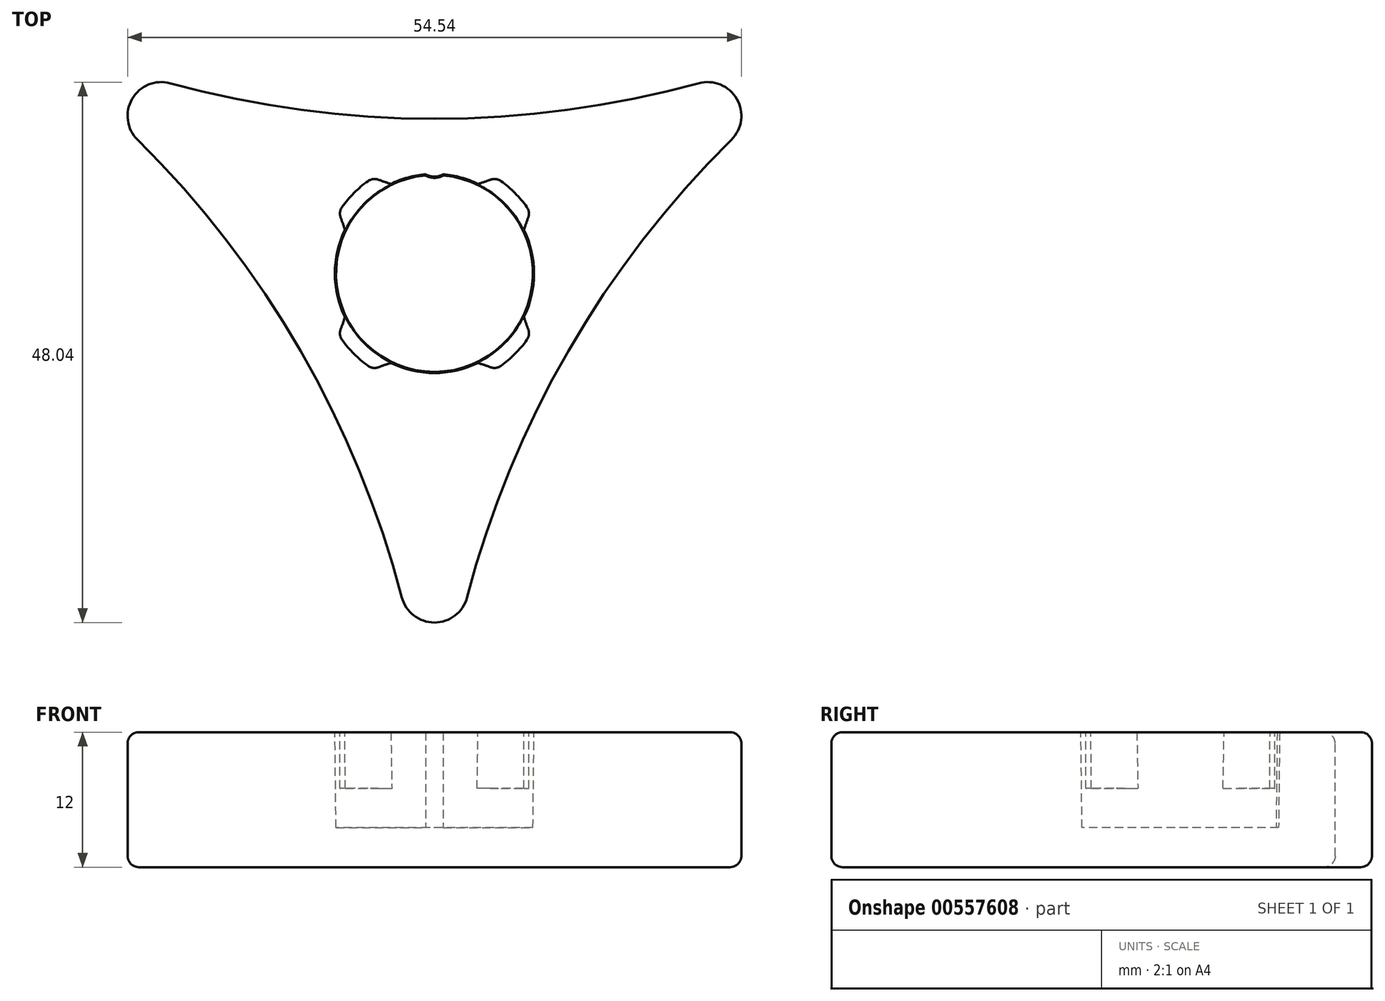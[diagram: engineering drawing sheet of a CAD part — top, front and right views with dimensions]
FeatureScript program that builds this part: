
annotation { "Feature Type Name" : "Feature", "Feature Type Description" : "" }
export const myFeature = defineFeature(function(context is Context, id is Id, definition is map)
    precondition{}
    {
        {
            assignVariable(context, id + "F0", {"name" : "height", "anyValue" : 8.5});
        }
        {
            assignVariable(context, id + "F1", {"name" : "middleThickness", "anyValue" : 3.5});
        }
        {
            var Q0;
            Q0=qCreatedBy(makeId("Top.planeOp"),FACE);
            var sketch = newSketch(context, id + "F2", { "sketchPlane" : qUnion([Q0])});
            skCircle(sketch, "E0", {"center": v(0, 0) * mm, "radius": 8.85 * mm});
            skSolve(sketch);
        }
        {
            var Q0;
            Q0=makeQuery(id+"F2.imprint","IMPRINT",FACE,{"disambiguationData":[TD([[makeQuery(id+"F2.imprint","IMPRINT",EDGE,{"derivedFrom":sQuery(id+"F2.wireOp",EDGE,"E0")}),1.0]])]});
            cPlane(context, id + "F3", {"entities" : qUnion([Q0]), "cplaneType" : CPlaneType.OFFSET, "offset" : (getVariable(context, 'height')) * mm, "width" : 150 * mm, "height" : 150 * mm});
        }
        {
            var Q0;
            Q0=makeQuery(id+"F2.imprint","IMPRINT",FACE,{"disambiguationData":[TD([[makeQuery(id+"F2.imprint","IMPRINT",EDGE,{"derivedFrom":sQuery(id+"F2.wireOp",EDGE,"E0")}),1.0]])]});
            var sketch = newSketch(context, id + "F4", { "sketchPlane" : qUnion([Q0])});
            skCircle(sketch, "E1", {"center": v(0, 0) * mm, "radius": 8.6 * mm, "construction": true});
            skArc(sketch, "E2", {"start": v(-0.78, 8.82) * mm, "mid": v(0, 8.6) * mm, "end": v(0.78, 8.82) * mm});
            skArc(sketch, "E3", {"start": v(0.78, 8.82) * mm, "mid": v(0, 8.85) * mm, "end": v(-0.78, 8.82) * mm});
            skSolve(sketch);
        }
        {
            var Q0;
            Q0=qCreatedBy(id+"F3.planeOp",FACE);
            var sketch = newSketch(context, id + "F5", { "sketchPlane" : qUnion([Q0])});
            skCircle(sketch, "E4", {"center": v(0, 0) * mm, "radius": 8.75 * mm});
            skSolve(sketch);
        }
        {
            var Q0;
            Q0=qCreatedBy(id+"F3.planeOp",FACE);
            var sketch = newSketch(context, id + "F6", { "sketchPlane" : qUnion([Q0])});
            skCircle(sketch, "E5", {"center": v(0, 0) * mm, "radius": 8.5 * mm, "construction": true});
            skArc(sketch, "E6", {"start": v(-0.77, 8.72) * mm, "mid": v(0, 8.5) * mm, "end": v(0.77, 8.72) * mm});
            skArc(sketch, "E7", {"start": v(0.77, 8.72) * mm, "mid": v(0, 8.75) * mm, "end": v(-0.77, 8.72) * mm});
            skSolve(sketch);
        }
        {
            var Q0;
            Q0 = qSketchRegion(id + "F2", true);
            var Q1;
            Q1 = qSketchRegion(id + "F5", true);
            loft(context, id + "F7", {"sheetProfilesArray" : [{ "sheetProfileEntities" : qUnion([Q0]) }, { "sheetProfileEntities" : qUnion([Q1]) }]});
        }
        {
            var Q1;
            Q1 = qSketchRegion(id + "F4", true);
            var Q2;
            Q2 = qSketchRegion(id + "F6", true);
            loft(context, id + "F8", {"operationType" : NewBodyOperationType.REMOVE, "sheetProfilesArray" : [{ "sheetProfileEntities" : qUnion([Q1]) }, { "sheetProfileEntities" : qUnion([Q2]) }]});
        }
        {
            var Q0;
            Q0=qCreatedBy(makeId("Front.planeOp"),FACE);
            var sketch = newSketch(context, id + "F9", { "sketchPlane" : qUnion([Q0])});
            skLineSegment(sketch, "E8", {"start": v(0, 0) * mm, "end": v(0, 8.15) * mm});
            skSolve(sketch);
        }
        {
            var Q0;
            Q0=qCreatedBy(makeId("Top.planeOp"),FACE);
            var sketch = newSketch(context, id + "F10", { "sketchPlane" : qUnion([Q0])});
            skCircle(sketch, "E9", {"center": v(0, 0) * mm, "radius": 13.75 * mm, "construction": true});
            skArc(sketch, "E10", {"start": v(-44.44, 25.66) * mm, "mid": v(0, 13.75) * mm, "end": v(44.44, 25.66) * mm});
            skArc(sketch, "E11.1.0", {"start": v(0, -51.32) * mm, "mid": v(-11.9, -6.88) * mm, "end": v(-44.44, 25.66) * mm});
            skArc(sketch, "E11.2.0", {"start": v(44.44, 25.66) * mm, "mid": v(11.9, -6.88) * mm, "end": v(0, -51.32) * mm});
            skSolve(sketch);
        }
        {
            var Q0;
            Q0 = qSketchRegion(id + "F10", true);
            extrude(context, id + "F11", {"entities" : qUnion([Q0]), "depth" : (getVariable(context, 'height') + getVariable(context, 'middleThickness')) * mm, "offsetDistance" : 25 * mm});
        }
        {
            var Q0;
            Q0=makeQuery(id+"F11.opExtrude","SWEPT_EDGE",EDGE,{"disambiguationData":[OSD([sQuery(id+"F10.wireOp",EDGE,"E10"),sQuery(id+"F10.wireOp",EDGE,"E11.2.0")])]});
            var Q1;
            Q1=makeQuery(id+"F11.opExtrude","SWEPT_EDGE",EDGE,{"disambiguationData":[OSD([sQuery(id+"F10.wireOp",EDGE,"E10"),sQuery(id+"F10.wireOp",EDGE,"E11.1.0")])]});
            var Q2;
            Q2=makeQuery(id+"F11.opExtrude","SWEPT_EDGE",EDGE,{"disambiguationData":[OSD([sQuery(id+"F10.wireOp",EDGE,"E11.1.0"),sQuery(id+"F10.wireOp",EDGE,"E11.2.0")])]});
            fillet(context, id + "F12", {"entities" : qUnion([Q0, Q1, Q2]), "radius" : 3 * mm, "tangentPropagation" : true, "allowEdgeOverflow" : false});
        }
        {
            var Q0;
            Q0=makeQuery(id+"F7.opLoft","SWEPT_BODY",BODY,{"disambiguationData":[OSD([makeQuery(id+"F2.imprint","IMPRINT",FACE,{"disambiguationData":[TD([[makeQuery(id+"F2.imprint","IMPRINT",EDGE,{"derivedFrom":sQuery(id+"F2.wireOp",EDGE,"E0")}),1.0]])]}),makeQuery(id+"F5.imprint","IMPRINT",FACE,{"disambiguationData":[TD([[makeQuery(id+"F5.imprint","IMPRINT",EDGE,{"derivedFrom":sQuery(id+"F5.wireOp",EDGE,"E4")}),1.0]])]})])]});
            var Q1;
            Q1=makeQuery(id+"F11.opExtrude","SWEPT_BODY",BODY,{"disambiguationData":[OSD([sQuery(id+"F10.wireOp",EDGE,"E10"),sQuery(id+"F10.wireOp",EDGE,"E11.1.0"),sQuery(id+"F10.wireOp",EDGE,"E11.2.0")])]});
            booleanBodies(context, id + "F13", {"operationType" : BooleanOperationType.SUBTRACTION, "tools" : qUnion([Q0]), "targets" : qUnion([Q1])});
        }
        {
            assignVariable(context, id + "F14", {"name" : "GoProKnobHeight", "anyValue" : 5});
        }
        {
            var Q0;
            Q0=makeQuery(id+"F11.opExtrude","CAP_FACE",FACE,{"disambiguationData":[OSD([sQuery(id+"F10.wireOp",EDGE,"E10"),sQuery(id+"F10.wireOp",EDGE,"E11.1.0"),sQuery(id+"F10.wireOp",EDGE,"E11.2.0")])],"isStart":true});
            var sketch = newSketch(context, id + "F15", { "sketchPlane" : qUnion([Q0])});
            skArc(sketch, "E12", {"start": v(5.9, -8.21) * mm, "mid": v(7.15, -7.15) * mm, "end": v(8.21, -5.9) * mm});
            skArc(sketch, "E13", {"start": v(-4.96, 8.33) * mm, "mid": v(0, 7.4) * mm, "end": v(4.96, 8.33) * mm});
            skArc(sketch, "E14.1.0", {"start": v(-8.33, -4.96) * mm, "mid": v(-7.4, 0) * mm, "end": v(-8.33, 4.96) * mm});
            skArc(sketch, "E14.2.0", {"start": v(4.96, -8.33) * mm, "mid": v(0, -7.4) * mm, "end": v(-4.96, -8.33) * mm});
            skArc(sketch, "E14.3.0", {"start": v(8.33, 4.96) * mm, "mid": v(7.4, 0) * mm, "end": v(8.33, -4.96) * mm});
            skPoint(sketch, "E15", {"position": v(5.44, 8.53) * mm});
            skPoint(sketch, "E16", {"position": v(5.44, -8.53) * mm});
            skArc(sketch, "E17.trimOffspring", {"start": v(-8.21, -5.9) * mm, "mid": v(-7.15, -7.15) * mm, "end": v(-5.9, -8.21) * mm});
            skArc(sketch, "E18.trimOffspring", {"start": v(-5.9, 8.21) * mm, "mid": v(-7.15, 7.15) * mm, "end": v(-8.21, 5.9) * mm});
            skArc(sketch, "E19.trimOffspring", {"start": v(8.21, 5.9) * mm, "mid": v(7.15, 7.15) * mm, "end": v(5.9, 8.21) * mm});
            skArc(sketch, "E20.filletArc", {"start": v(4.96, -8.33) * mm, "mid": v(5.45, -8.4) * mm, "end": v(5.9, -8.21) * mm});
            skPoint(sketch, "E21.visualSharp", {"position": v(8.53, -5.44) * mm});
            skArc(sketch, "E21.filletArc", {"start": v(8.21, -5.9) * mm, "mid": v(8.4, -5.45) * mm, "end": v(8.33, -4.96) * mm});
            skPoint(sketch, "E22.visualSharp", {"position": v(8.53, 5.44) * mm});
            skArc(sketch, "E22.filletArc", {"start": v(8.33, 4.96) * mm, "mid": v(8.4, 5.45) * mm, "end": v(8.21, 5.9) * mm});
            skArc(sketch, "E23.filletArc", {"start": v(5.9, 8.21) * mm, "mid": v(5.45, 8.4) * mm, "end": v(4.96, 8.33) * mm});
            skPoint(sketch, "E24.visualSharp", {"position": v(-5.44, 8.53) * mm});
            skArc(sketch, "E24.filletArc", {"start": v(-4.96, 8.33) * mm, "mid": v(-5.45, 8.4) * mm, "end": v(-5.9, 8.21) * mm});
            skPoint(sketch, "E25.visualSharp", {"position": v(-8.53, 5.44) * mm});
            skArc(sketch, "E25.filletArc", {"start": v(-8.21, 5.9) * mm, "mid": v(-8.4, 5.45) * mm, "end": v(-8.33, 4.96) * mm});
            skPoint(sketch, "E26.visualSharp", {"position": v(-8.53, -5.44) * mm});
            skArc(sketch, "E26.filletArc", {"start": v(-8.33, -4.96) * mm, "mid": v(-8.4, -5.45) * mm, "end": v(-8.21, -5.9) * mm});
            skPoint(sketch, "E27.visualSharp", {"position": v(-5.44, -8.53) * mm});
            skArc(sketch, "E27.filletArc", {"start": v(-5.9, -8.21) * mm, "mid": v(-5.45, -8.4) * mm, "end": v(-4.96, -8.33) * mm});
            skSolve(sketch);
        }
        {
            var Q0;
            Q0 = qSketchRegion(id + "F15", true);
            extrude(context, id + "F16", {"entities" : qUnion([Q0]), "operationType" : NewBodyOperationType.REMOVE, "oppositeDirection" : true, "depth" : (getVariable(context, 'GoProKnobHeight')) * mm, "offsetDistance" : 25 * mm});
        }
        {
            var Q0;
            Q0=makeQuery(id+"F11.opExtrude","CAP_FACE",FACE,{"disambiguationData":[OSD([sQuery(id+"F10.wireOp",EDGE,"E10"),sQuery(id+"F10.wireOp",EDGE,"E11.1.0"),sQuery(id+"F10.wireOp",EDGE,"E11.2.0")])],"isStart":true});
            cPlane(context, id + "F17", {"entities" : qUnion([Q0]), "cplaneType" : CPlaneType.OFFSET, "offset" : ((getVariable(context, 'height') + getVariable(context, 'middleThickness')) / 2) * mm, "oppositeDirection" : true, "width" : 150 * mm, "height" : 150 * mm});
        }
        {
            var Q0;
            Q0=qCreatedBy(id+"F17.planeOp",FACE);
            var sketch = newSketch(context, id + "F18", { "sketchPlane" : qUnion([Q0])});
            skLineSegment(sketch, "E28", {"start": v(0, 45.44) * mm, "end": v(0, -39.08) * mm, "construction": true});
            skSolve(sketch);
        }
        {
            var Q0;
            Q0=makeQuery(id+"F11.opExtrude","SWEPT_BODY",BODY,{"disambiguationData":[OSD([sQuery(id+"F10.wireOp",EDGE,"E10"),sQuery(id+"F10.wireOp",EDGE,"E11.1.0"),sQuery(id+"F10.wireOp",EDGE,"E11.2.0")])]});
            var Q1;
            Q1=sQuery(id+"F18.wireOp",EDGE,"E28");
            transform(context, id + "F19", {"entities" : qUnion([Q0]), "transformType" : TransformType.ROTATION, "transformAxis" : qUnion([Q1]), "angle" : 180 * degree, "makeCopy" : false});
        }
        {
            var Q0;
            Q0=makeQuery(id+"F11.opExtrude","CAP_EDGE",EDGE,{"disambiguationData":[OSD([sQuery(id+"F10.wireOp",EDGE,"E10")])],"isStart":true});
            var Q1;
            Q1=makeQuery(id+"F11.opExtrude","CAP_EDGE",EDGE,{"disambiguationData":[OSD([sQuery(id+"F10.wireOp",EDGE,"E10")])],"isStart":false});
            fillet(context, id + "F20", {"entities" : qUnion([Q0, Q1]), "radius" : 1 * mm, "tangentPropagation" : true, "allowEdgeOverflow" : false});
        }
    });
